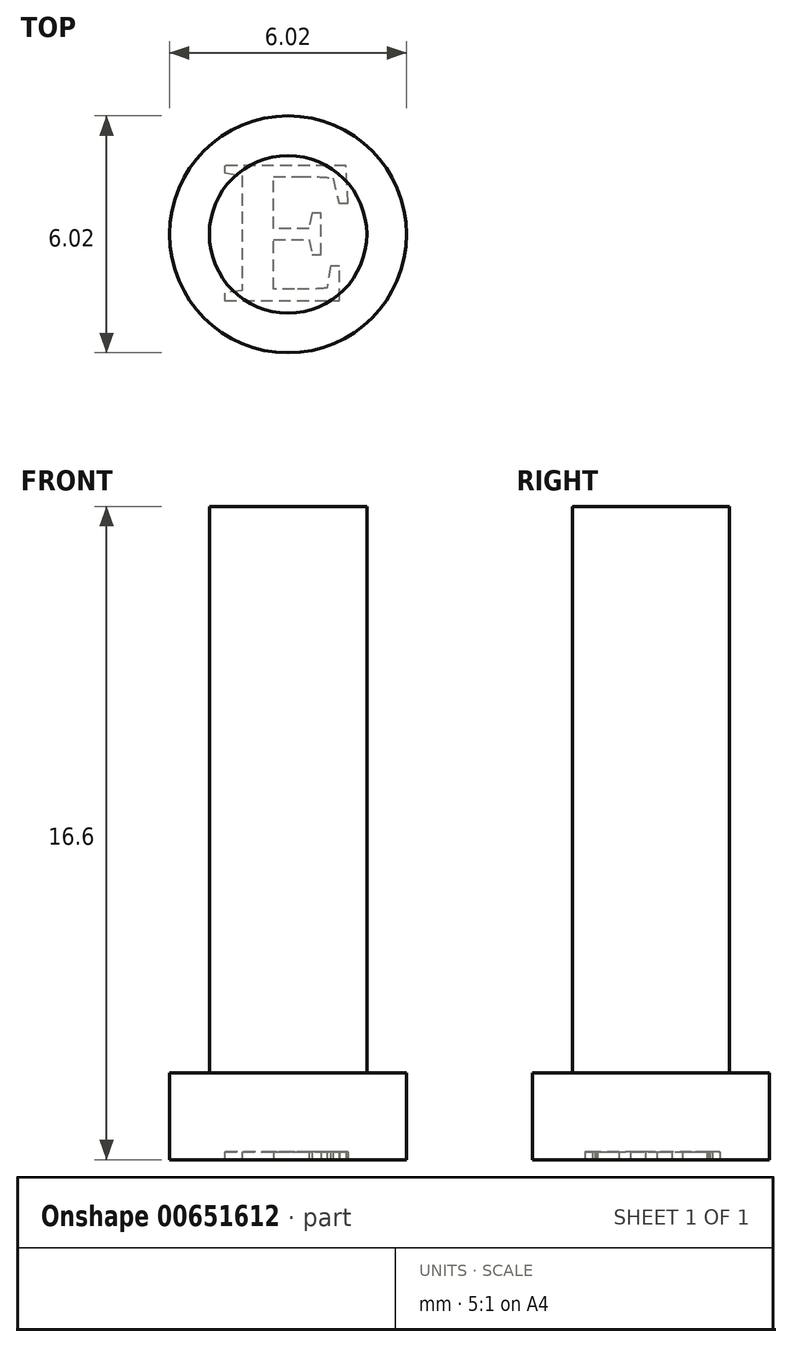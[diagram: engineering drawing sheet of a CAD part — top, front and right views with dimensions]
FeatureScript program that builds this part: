
annotation { "Feature Type Name" : "Feature", "Feature Type Description" : "" }
export const myFeature = defineFeature(function(context is Context, id is Id, definition is map)
    precondition{}
    {
        {
            var Q0;
            Q0=qCreatedBy(makeId("Top.planeOp"),FACE);
            var sketch = newSketch(context, id + "F0", { "sketchPlane" : qUnion([Q0])});
            skCircle(sketch, "E0", {"center": v(0, 0) * mm, "radius": 2 * mm});
            skSolve(sketch);
        }
        {
            var Q0;
            Q0=makeQuery(id+"F0.imprint","IMPRINT",FACE,{"disambiguationData":[TD([[makeQuery(id+"F0.imprint","IMPRINT",EDGE,{"derivedFrom":sQuery(id+"F0.wireOp",EDGE,"E0")}),1.0]])]});
            extrude(context, id + "F1", {"entities" : qUnion([Q0]), "depth" : 14.4 * mm});
        }
        {
            var Q0;
            Q0=makeQuery(id+"F1.opExtrude","CAP_FACE",FACE,{"disambiguationData":[OSD([sQuery(id+"F0.wireOp",EDGE,"E0")])],"isStart":true});
            var sketch = newSketch(context, id + "F2", { "sketchPlane" : qUnion([Q0])});
            skCircle(sketch, "E1", {"center": v(0, 0) * mm, "radius": 3.01 * mm});
            skSolve(sketch);
        }
        {
            var Q0;
            Q0=makeQuery(id+"F2.imprint","IMPRINT",FACE,{"disambiguationData":[TD([[makeQuery(id+"F2.imprint","IMPRINT",EDGE,{"derivedFrom":makeQuery(id+"F1.opExtrude","CAP_EDGE",EDGE,{"disambiguationData":[OSD([sQuery(id+"F0.wireOp",EDGE,"E0")])],"isStart":true})}),-1.0]])]});
            var Q1;
            Q1=makeQuery(id+"F2.imprint","IMPRINT",FACE,{"disambiguationData":[TD([[makeQuery(id+"F2.imprint","IMPRINT",EDGE,{"derivedFrom":sQuery(id+"F2.wireOp",EDGE,"E1")}),1.0]])]});
            extrude(context, id + "F3", {"entities" : qUnion([Q0, Q1]), "operationType" : NewBodyOperationType.ADD, "depth" : 2.2 * mm});
        }
        {
            var Q0;
            Q0=makeQuery(id+"F3.opExtrude","CAP_FACE",FACE,{"disambiguationData":[OSD([sQuery(id+"F2.wireOp",EDGE,"E1")])],"isStart":false});
            var sketch = newSketch(context, id + "F4", { "sketchPlane" : qUnion([Q0])});
            skText(sketch, "E2", { "text": "E", "fontName": "Tinos-Bold.ttf"});
            const initialGuessF4  = {"E2": [-0.0017, -0.00175, 1, 0, 0.00377]};
            skSetInitialGuess(sketch, initialGuessF4);
            skSolve(sketch);
        }
        {
            var Q0;
            Q0=makeQuery(id+"F4.imprint","IMPRINT",FACE,{"disambiguationData":[TD([[makeQuery(id+"F4.imprint","IMPRINT",EDGE,{"derivedFrom":sQuery(id+"F4.wireOp",EDGE,"E2.sketch_text.stroke-0")}),-1.0]])]});
            extrude(context, id + "F5", {"entities" : qUnion([Q0]), "operationType" : NewBodyOperationType.REMOVE, "oppositeDirection" : true, "depth" : 0.2 * mm});
        }
    });
